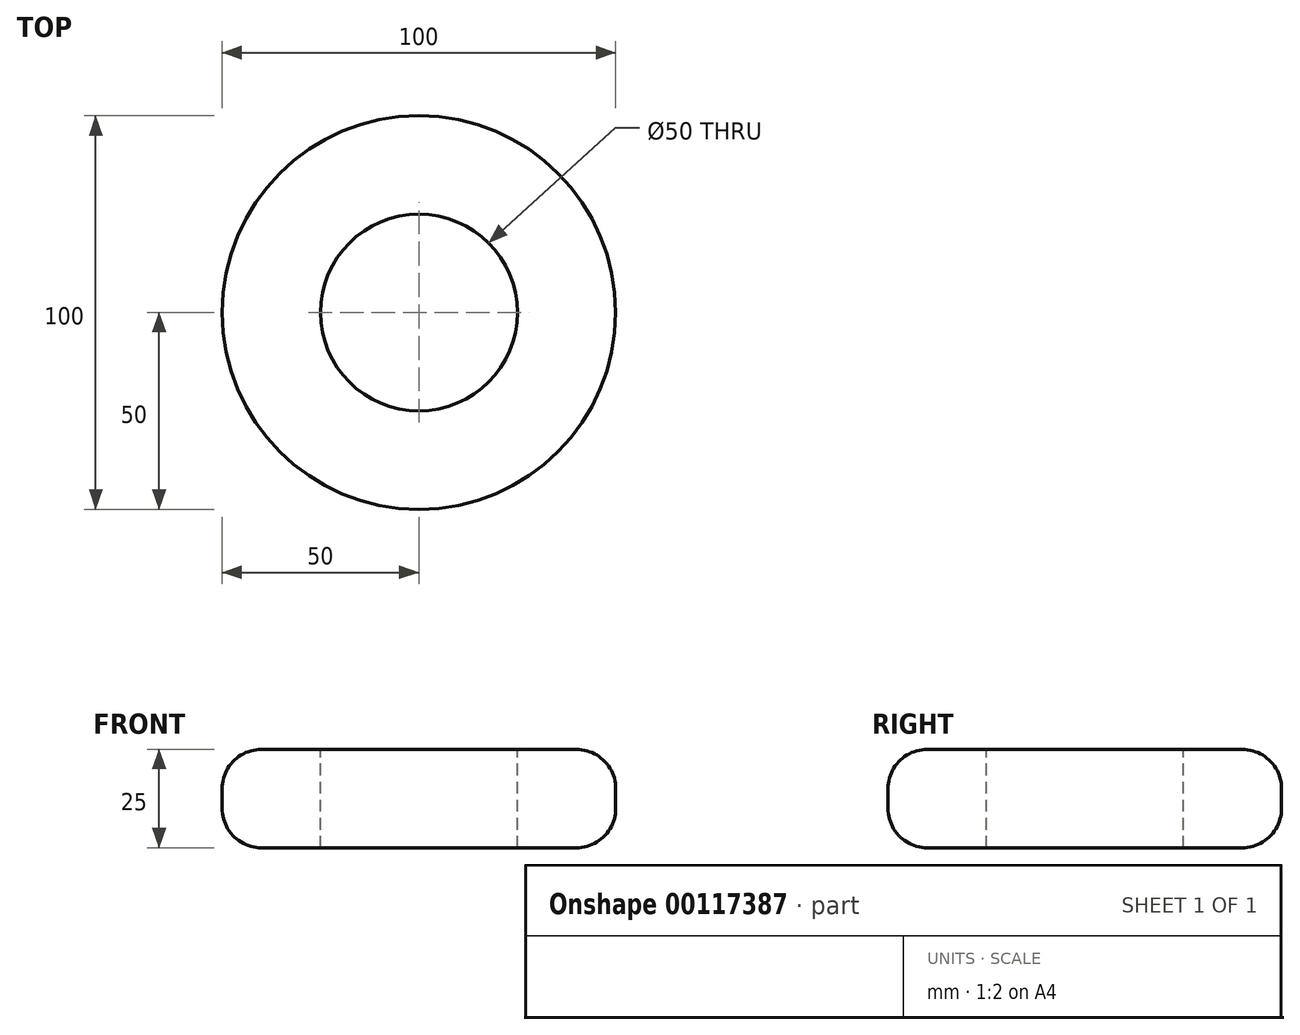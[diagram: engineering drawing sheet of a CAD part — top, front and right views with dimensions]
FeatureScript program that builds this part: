
annotation { "Feature Type Name" : "Feature", "Feature Type Description" : "" }
export const myFeature = defineFeature(function(context is Context, id is Id, definition is map)
    precondition{}
    {
        {
            var Q0;
            Q0=qCreatedBy(makeId("Top.planeOp"),FACE);
            var sketch = newSketch(context, id + "F0", { "sketchPlane" : qUnion([Q0])});
            skCircle(sketch, "E0", {"center": v(0, 0) * mm, "radius": 50 * mm});
            skSolve(sketch);
        }
        {
            var Q0;
            Q0 = qSketchRegion(id + "F0", true);
            extrude(context, id + "F1", {"entities" : qUnion([Q0]), "depth" : 25 * mm, "symmetric" : true});
        }
        {
            var Q0;
            Q0=makeQuery(id+"F1.opExtrude","CAP_FACE",FACE,{"disambiguationData":[OSD([sQuery(id+"F0.wireOp",EDGE,"E0")])],"isStart":false});
            var sketch = newSketch(context, id + "F2", { "sketchPlane" : qUnion([Q0])});
            skCircle(sketch, "E1", {"center": v(0, 0) * mm, "radius": 25 * mm});
            skSolve(sketch);
        }
        {
            var Q0;
            Q0 = qSketchRegion(id + "F2", true);
            extrude(context, id + "F3", {"entities" : qUnion([Q0]), "operationType" : NewBodyOperationType.REMOVE, "oppositeDirection" : true, "depth" : 25 * mm});
        }
        {
            var Q0;
            Q0=makeQuery(id+"F1.opExtrude","CAP_EDGE",EDGE,{"disambiguationData":[OSD([sQuery(id+"F0.wireOp",EDGE,"E0")])],"isStart":false});
            var Q1;
            Q1=makeQuery(id+"F1.opExtrude","CAP_EDGE",EDGE,{"disambiguationData":[OSD([sQuery(id+"F0.wireOp",EDGE,"E0")])],"isStart":true});
            var Q2;
            Q2=makeQuery(id+"F3.boolean.opBoolean","COPY",EDGE,{"derivedFrom":makeQuery(id+"F3.opExtrude","CAP_EDGE",EDGE,{"disambiguationData":[OSD([sQuery(id+"F2.wireOp",EDGE,"E1")])],"isStart":true})});
            var Q3;
            Q3=makeQuery(id+"F3.boolean.opBoolean","COPY",EDGE,{"derivedFrom":makeQuery(id+"F3.opExtrude","CAP_EDGE",EDGE,{"disambiguationData":[OSD([sQuery(id+"F2.wireOp",EDGE,"E1")])],"isStart":false})});
            fillet(context, id + "F4", {"entities" : qUnion([Q0, Q1, Q2, Q3]), "radius" : 10 * mm, "tangentPropagation" : true, "allowEdgeOverflow" : false});
        }
    });
